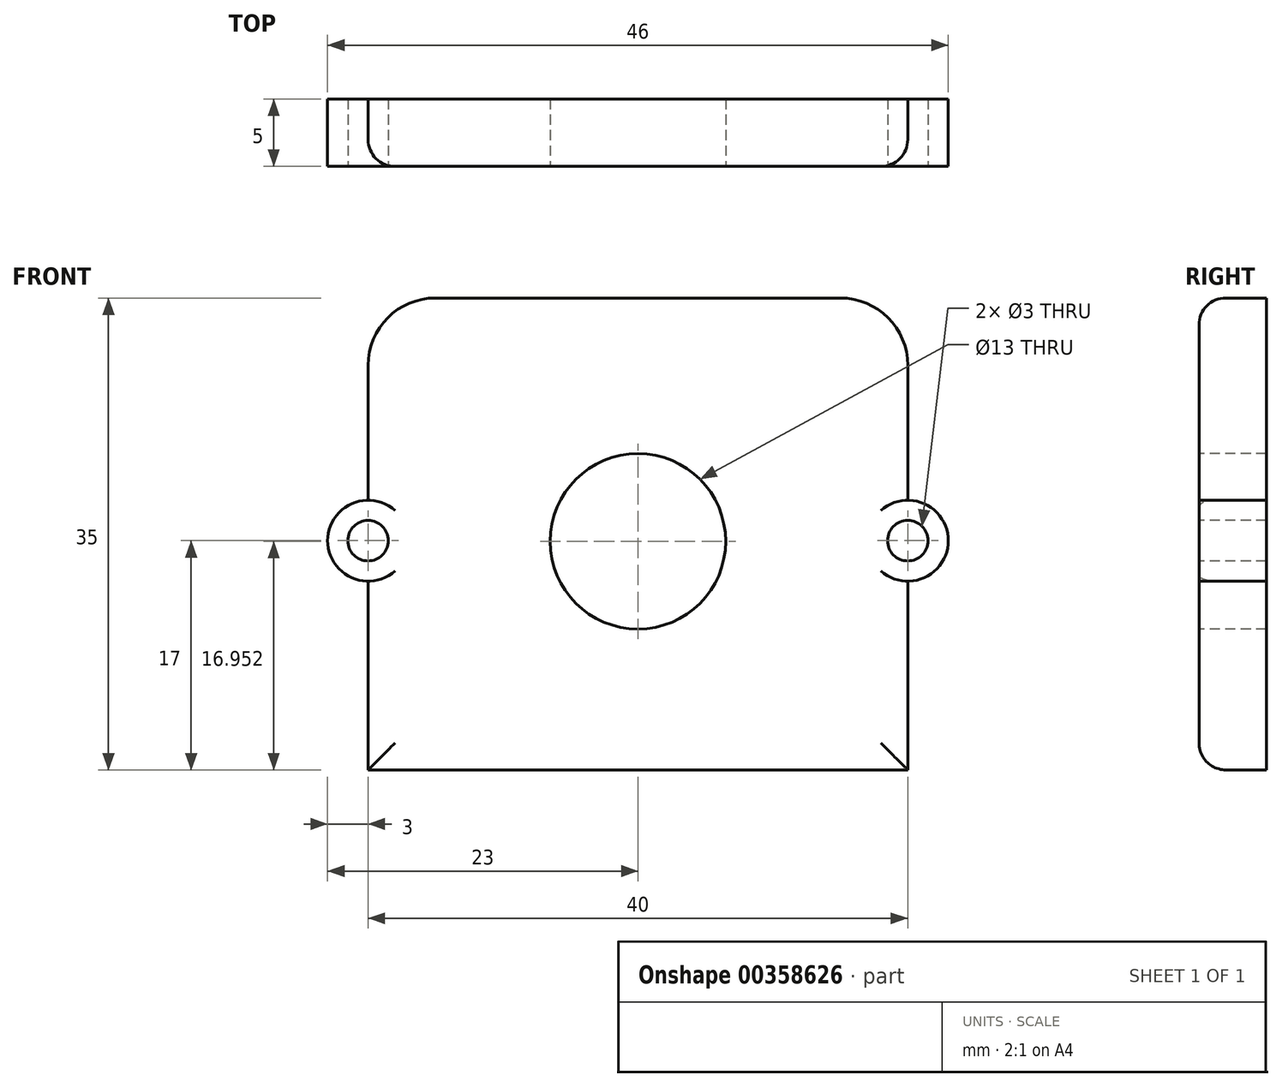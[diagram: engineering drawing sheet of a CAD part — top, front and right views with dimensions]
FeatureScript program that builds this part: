
annotation { "Feature Type Name" : "Feature", "Feature Type Description" : "" }
export const myFeature = defineFeature(function(context is Context, id is Id, definition is map)
    precondition{}
    {
        {
            var Q0;
            Q0=qCreatedBy(makeId("Front.planeOp"),FACE);
            var sketch = newSketch(context, id + "F0", { "sketchPlane" : qUnion([Q0])});
            skLineSegment(sketch, "E0.bottom", {"start": v(0, 0) * mm, "end": v(40, 0) * mm});
            skLineSegment(sketch, "E0.top", {"start": v(5, 35) * mm, "end": v(35, 35) * mm});
            skLineSegment(sketch, "E0.left", {"start": v(0, 0) * mm, "end": v(0, 14) * mm});
            skLineSegment(sketch, "E0.right", {"start": v(40, 0) * mm, "end": v(40, 14) * mm});
            skArc(sketch, "E1", {"start": v(0, 20) * mm, "mid": v(-3, 17) * mm, "end": v(0, 14) * mm});
            skArc(sketch, "E2", {"start": v(40, 14) * mm, "mid": v(43, 17) * mm, "end": v(40, 20) * mm});
            skPoint(sketch, "E3.visualSharp", {"position": v(0, 35) * mm});
            skArc(sketch, "E3.filletArc", {"start": v(5, 35) * mm, "mid": v(1.46, 33.54) * mm, "end": v(0, 30) * mm});
            skPoint(sketch, "E4.visualSharp", {"position": v(40, 35) * mm});
            skArc(sketch, "E4.filletArc", {"start": v(40, 30) * mm, "mid": v(38.54, 33.54) * mm, "end": v(35, 35) * mm});
            skLineSegment(sketch, "E5.trimOffspring", {"start": v(0, 20) * mm, "end": v(0, 30) * mm});
            skLineSegment(sketch, "E6.trimOffspring", {"start": v(40, 20) * mm, "end": v(40, 30) * mm});
            skSolve(sketch);
        }
        {
            var Q0;
            Q0=makeQuery(id+"F0.imprint","IMPRINT",FACE,{"disambiguationData":[TD([[makeQuery(id+"F0.imprint","IMPRINT",EDGE,{"derivedFrom":sQuery(id+"F0.wireOp",EDGE,"E0.bottom")}),1.0]])]});
            extrude(context, id + "F1", {"entities" : qUnion([Q0]), "depth" : 5 * mm});
        }
        {
            var Q0;
            Q0=makeQuery(id+"F1.opExtrude","CAP_FACE",FACE,{"disambiguationData":[OSD([sQuery(id+"F0.wireOp",EDGE,"E0.bottom"),sQuery(id+"F0.wireOp",EDGE,"E0.top"),sQuery(id+"F0.wireOp",EDGE,"E0.left"),sQuery(id+"F0.wireOp",EDGE,"E0.right"),sQuery(id+"F0.wireOp",EDGE,"E1"),sQuery(id+"F0.wireOp",EDGE,"E2"),sQuery(id+"F0.wireOp",EDGE,"E3.filletArc"),sQuery(id+"F0.wireOp",EDGE,"E4.filletArc"),sQuery(id+"F0.wireOp",EDGE,"E5.trimOffspring"),sQuery(id+"F0.wireOp",EDGE,"E6.trimOffspring")])],"isStart":false});
            var sketch = newSketch(context, id + "F2", { "sketchPlane" : qUnion([Q0])});
            skCircle(sketch, "E7", {"center": v(0, 17) * mm, "radius": 1.5 * mm});
            skCircle(sketch, "E8", {"center": v(40, 17) * mm, "radius": 1.5 * mm});
            skSolve(sketch);
        }
        {
            var Q0;
            Q0 = qSketchRegion(id + "F2", true);
            extrude(context, id + "F3", {"entities" : qUnion([Q0]), "operationType" : NewBodyOperationType.REMOVE, "oppositeDirection" : true, "depth" : 25 * mm});
        }
        {
            var Q0;
            Q0=makeQuery(id+"F1.opExtrude","CAP_FACE",FACE,{"disambiguationData":[OSD([sQuery(id+"F0.wireOp",EDGE,"E0.bottom"),sQuery(id+"F0.wireOp",EDGE,"E0.top"),sQuery(id+"F0.wireOp",EDGE,"E0.left"),sQuery(id+"F0.wireOp",EDGE,"E0.right"),sQuery(id+"F0.wireOp",EDGE,"E1"),sQuery(id+"F0.wireOp",EDGE,"E2"),sQuery(id+"F0.wireOp",EDGE,"E3.filletArc"),sQuery(id+"F0.wireOp",EDGE,"E4.filletArc"),sQuery(id+"F0.wireOp",EDGE,"E5.trimOffspring"),sQuery(id+"F0.wireOp",EDGE,"E6.trimOffspring")])],"isStart":false});
            var sketch = newSketch(context, id + "F4", { "sketchPlane" : qUnion([Q0])});
            skCircle(sketch, "E9", {"center": v(20, 16.95) * mm, "radius": 6.5 * mm});
            skPoint(sketch, "E9.centerSnap0", {"position": v(20, 35) * mm});
            skSolve(sketch);
        }
        {
            var Q0;
            Q0 = qSketchRegion(id + "F4", true);
            extrude(context, id + "F5", {"entities" : qUnion([Q0]), "operationType" : NewBodyOperationType.REMOVE, "oppositeDirection" : true, "depth" : 25 * mm});
        }
        {
            var Q0;
            Q0=makeQuery(id+"F1.opExtrude","CAP_EDGE",EDGE,{"disambiguationData":[OSD([sQuery(id+"F0.wireOp",EDGE,"E5.trimOffspring")])],"isStart":false});
            var Q1;
            Q1=makeQuery(id+"F1.opExtrude","CAP_EDGE",EDGE,{"disambiguationData":[OSD([sQuery(id+"F0.wireOp",EDGE,"E0.right")])],"isStart":false});
            var Q2;
            Q2=makeQuery(id+"F1.opExtrude","CAP_EDGE",EDGE,{"disambiguationData":[OSD([sQuery(id+"F0.wireOp",EDGE,"E0.bottom")])],"isStart":false});
            var Q3;
            Q3=makeQuery(id+"F1.opExtrude","CAP_EDGE",EDGE,{"disambiguationData":[OSD([sQuery(id+"F0.wireOp",EDGE,"E0.left")])],"isStart":false});
            fillet(context, id + "F6", {"entities" : qUnion([Q0, Q1, Q2, Q3]), "radius" : 2 * mm, "tangentPropagation" : true, "allowEdgeOverflow" : false});
        }
    });
